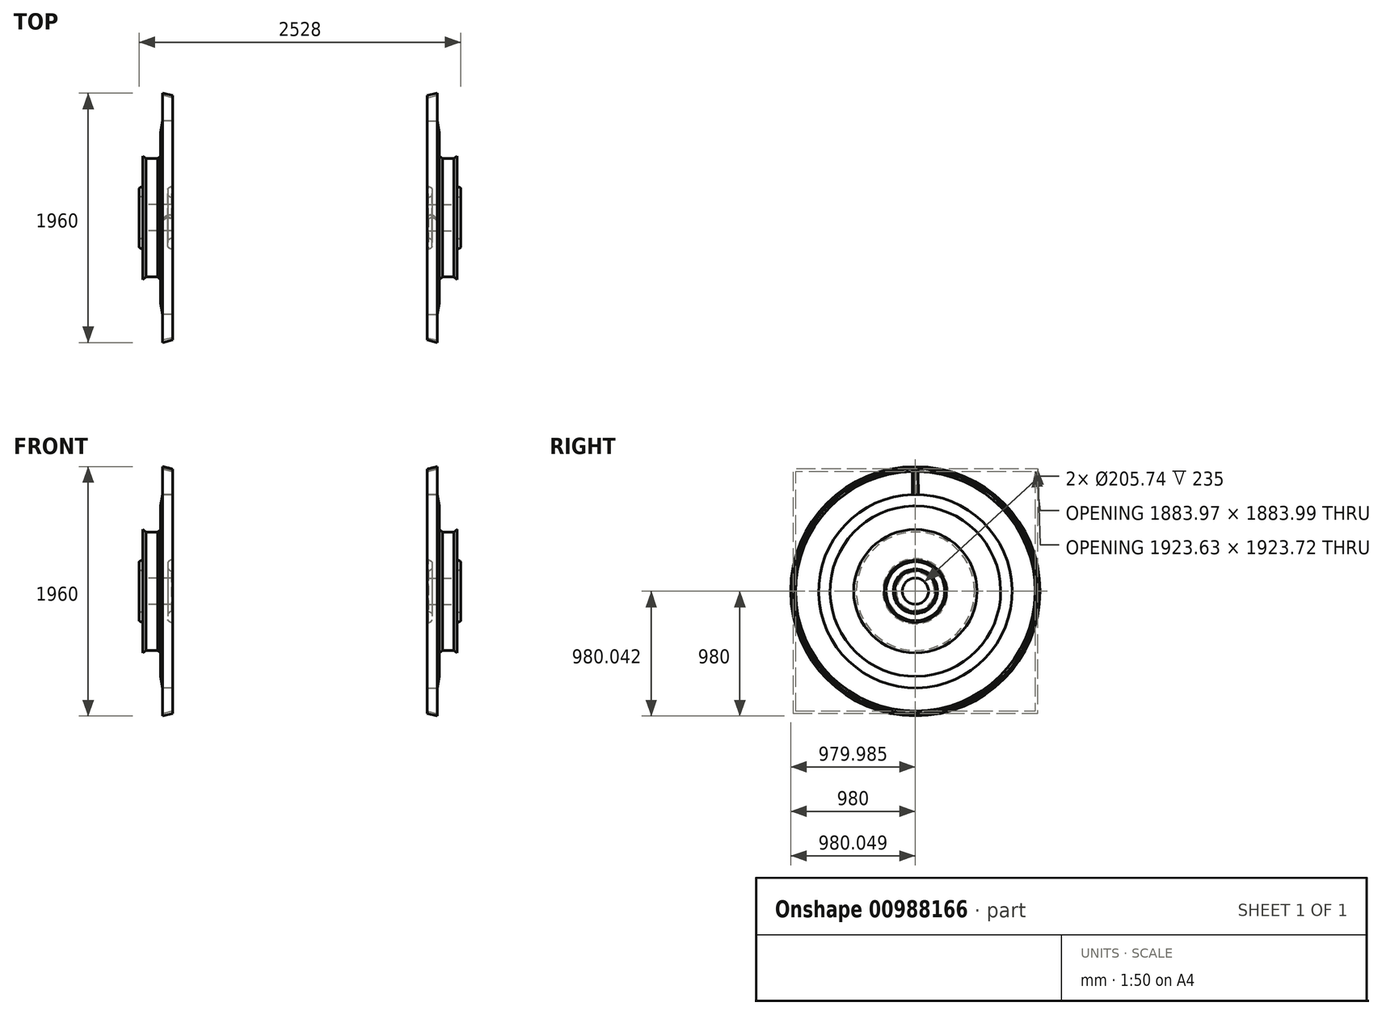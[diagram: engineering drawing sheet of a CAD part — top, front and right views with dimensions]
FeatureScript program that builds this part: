
annotation { "Feature Type Name" : "Feature", "Feature Type Description" : "" }
export const myFeature = defineFeature(function(context is Context, id is Id, definition is map)
    precondition{}
    {
        {
            var Q0;
            Q0=qCreatedBy(makeId("Top.planeOp"),FACE);
            var sketch = newSketch(context, id + "F0", { "sketchPlane" : qUnion([Q0])});
            skLineSegment(sketch, "E0", {"start": v(-458.73, 0) * mm, "end": v(0, 0) * mm, "construction": true});
            skLineSegment(sketch, "E1", {"start": v(0, 760) * mm, "end": v(-80, 760) * mm});
            skLineSegment(sketch, "E2", {"start": v(-120, 465) * mm, "end": v(-210, 465) * mm});
            skLineSegment(sketch, "E3", {"start": v(-210, 465) * mm, "end": v(-235, 485) * mm});
            skLineSegment(sketch, "E4", {"start": v(-235, 485) * mm, "end": v(-235, 243.87) * mm});
            skLineSegment(sketch, "E5", {"start": v(-235, 102.87) * mm, "end": v(0, 102.87) * mm});
            skLineSegment(sketch, "E6", {"start": v(0, 102.87) * mm, "end": v(0, 157.87) * mm});
            skLineSegment(sketch, "E7", {"start": v(-80, 980) * mm, "end": v(-80, 962) * mm});
            skLineSegment(sketch, "E8", {"start": v(-80, 962) * mm, "end": v(0, 942) * mm});
            skLineSegment(sketch, "E9", {"start": v(0, 942) * mm, "end": v(0, 960) * mm});
            skLineSegment(sketch, "E10", {"start": v(0, 960) * mm, "end": v(-80, 980) * mm});
            skLineSegment(sketch, "E11", {"start": v(-80, 760) * mm, "end": v(-80, 962) * mm, "construction": true});
            skLineSegment(sketch, "E12", {"start": v(-95, 485) * mm, "end": v(-95, 670) * mm});
            skLineSegment(sketch, "E13", {"start": v(-95, 670) * mm, "end": v(-80, 760) * mm});
            skLineSegment(sketch, "E14", {"start": v(-95, 485) * mm, "end": v(-120, 465) * mm});
            skLineSegment(sketch, "E15", {"start": v(-95, 485) * mm, "end": v(-235, 485) * mm, "construction": true});
            skArc(sketch, "E16", {"start": v(-235, 161.87) * mm, "mid": v(-250.7, 165) * mm, "end": v(-264, 173.89) * mm});
            skLineSegment(sketch, "E17", {"start": v(-264, 231.85) * mm, "end": v(-264, 173.89) * mm});
            skArc(sketch, "E18.trimOffspring", {"start": v(-264, 231.85) * mm, "mid": v(-250.7, 240.75) * mm, "end": v(-235, 243.87) * mm});
            skLineSegment(sketch, "E19.trimOffspring", {"start": v(-235, 161.87) * mm, "end": v(-235, 102.87) * mm});
            skArc(sketch, "E20", {"start": v(-235, 161.87) * mm, "mid": v(-276, 202.87) * mm, "end": v(-235, 243.87) * mm, "construction": true});
            skLineSegment(sketch, "E21", {"start": v(-235, 202.87) * mm, "end": v(0, 202.87) * mm, "construction": true});
            skArc(sketch, "E22", {"start": v(0, 157.87) * mm, "mid": v(-22.53, 163.91) * mm, "end": v(-39, 180.42) * mm});
            skLineSegment(sketch, "E23", {"start": v(-39, 225.32) * mm, "end": v(-39, 180.42) * mm});
            skArc(sketch, "E24.trimOffspring", {"start": v(-39, 225.32) * mm, "mid": v(-22.53, 241.83) * mm, "end": v(0, 247.87) * mm});
            skLineSegment(sketch, "E25.trimOffspring", {"start": v(0, 247.87) * mm, "end": v(0, 760) * mm});
            skArc(sketch, "E26", {"start": v(0, 157.87) * mm, "mid": v(-45, 202.87) * mm, "end": v(0, 247.87) * mm, "construction": true});
            skSolve(sketch);
        }
        {
            var Q0;
            Q0=makeQuery(id+"F0.imprint","IMPRINT",FACE,{"disambiguationData":[TD([[makeQuery(id+"F0.imprint","IMPRINT",EDGE,{"derivedFrom":sQuery(id+"F0.wireOp",EDGE,"E7")}),1.0]])]});
            var Q1;
            Q1=makeQuery(id+"F0.imprint","IMPRINT",FACE,{"disambiguationData":[TD([[makeQuery(id+"F0.imprint","IMPRINT",EDGE,{"derivedFrom":sQuery(id+"F0.wireOp",EDGE,"E1")}),1.0]])]});
            var Q2;
            Q2=sQuery(id+"F0.wireOp",EDGE,"E0");
            revolve(context, id + "F1", {"surfaceOperationType" : NewSurfaceOperationType.NEW, "entities" : qUnion([Q0, Q1]), "axis" : qUnion([Q2]), "revolveType" : RevolveType.FULL});
        }
        {
            var Q0;
            Q0=makeQuery(id+"F1.opRevolve","SWEPT_EDGE",EDGE,{"disambiguationData":[OSD([sQuery(id+"F0.wireOp",EDGE,"E24.trimOffspring"),sQuery(id+"F0.wireOp",EDGE,"E25.trimOffspring")])]});
            var Q1;
            Q1=makeQuery(id+"F1.opRevolve","SWEPT_EDGE",EDGE,{"disambiguationData":[OSD([sQuery(id+"F0.wireOp",EDGE,"E6"),sQuery(id+"F0.wireOp",EDGE,"E22")])]});
            chamfer(context, id + "F2", {"entities" : qUnion([Q0, Q1]), "width" : 9 * mm, "tangentPropagation" : true});
        }
        {
            var Q0;
            Q0=qCreatedBy(makeId("Right.planeOp"),FACE);
            var sketch = newSketch(context, id + "F3", { "sketchPlane" : qUnion([Q0])});
            skLineSegment(sketch, "E27", {"start": v(0, 0) * mm, "end": v(0, 760) * mm, "construction": true});
            skLineSegment(sketch, "E28", {"start": v(0, 0) * mm, "end": v(0, 960) * mm, "construction": true});
            skCircle(sketch, "E29.0", {"center": v(0, 0) * mm, "radius": 960 * mm, "construction": true});
            skCircle(sketch, "E30.0", {"center": v(0, 0) * mm, "radius": 760 * mm, "construction": true});
            skSolve(sketch);
        }
        {
            var Q0;
            Q0=qCreatedBy(makeId("Front.planeOp"),FACE);
            var sketch = newSketch(context, id + "F4", { "sketchPlane" : qUnion([Q0])});
            skLineSegment(sketch, "E31", {"start": v(-80, 980) * mm, "end": v(0, 960) * mm, "construction": true});
            skLineSegment(sketch, "E32", {"start": v(-40, 970) * mm, "end": v(-52.13, 921.5) * mm, "construction": true});
            skSolve(sketch);
        }
        {
            var Q0;
            Q0=sQuery(id+"F4.wireOp",VERTEX,"E32.start");
            var Q1;
            Q1=sQuery(id+"F4.wireOp",EDGE,"E32");
            cPlane(context, id + "F5", {"entities" : qUnion([Q0, Q1]), "cplaneType" : CPlaneType.LINE_POINT, "offset" : 25 * mm, "width" : 150 * mm, "height" : 150 * mm});
        }
        {
            var Q0;
            Q0=sQuery(id+"F3.wireOp",VERTEX,"E27.end");
            var Q1;
            Q1=sQuery(id+"F3.wireOp",EDGE,"E28");
            cPlane(context, id + "F6", {"entities" : qUnion([Q0, Q1]), "cplaneType" : CPlaneType.LINE_POINT, "offset" : 25 * mm, "width" : 150 * mm, "height" : 150 * mm});
        }
        {
            var Q0;
            Q0=qCreatedBy(id+"F6.planeOp",FACE);
            cPlane(context, id + "F7", {"entities" : qUnion([Q0]), "cplaneType" : CPlaneType.OFFSET, "offset" : 1 * mm, "oppositeDirection" : true, "width" : 150 * mm, "height" : 150 * mm});
        }
        {
            var Q0;
            Q0=qCreatedBy(id+"F5.planeOp",FACE);
            cPlane(context, id + "F8", {"entities" : qUnion([Q0]), "cplaneType" : CPlaneType.OFFSET, "offset" : 4 * mm, "width" : 150 * mm, "height" : 150 * mm});
        }
        {
            var Q0;
            Q0=qCreatedBy(id+"F7.planeOp",FACE);
            var sketch = newSketch(context, id + "F9", { "sketchPlane" : qUnion([Q0])});
            skLineSegment(sketch, "E33.0", {"start": v(-80, -760) * mm, "end": v(-80, 760) * mm, "construction": true});
            skLineSegment(sketch, "E34.0", {"start": v(0, 760) * mm, "end": v(0, -760) * mm, "construction": true});
            skLineSegment(sketch, "E35", {"start": v(0, 0) * mm, "end": v(0, 15) * mm});
            skLineSegment(sketch, "E36", {"start": v(-80, -11.9) * mm, "end": v(-80, -21.9) * mm});
            skFitSpline(sketch, "E37", {"points": [v(0, 15) * mm, v(-27.24, 23.1) * mm, v(-53.2, 15) * mm, v(-80, -11.9) * mm], "startDerivative": vector(-98.33, 77.82) * mm, "endDerivative": vector(-58.12, -78.29) * mm});
            skFitSpline(sketch, "E38", {"points": [v(0, 0) * mm, v(-12.16, -4.34) * mm, v(-33.61, 3.06) * mm, v(-80, -21.9) * mm], "startDerivative": vector(-36.35, -51.97) * mm, "endDerivative": vector(-93.61, -87.67) * mm});
            skSolve(sketch);
        }
        {
            var Q0;
            Q0=qCreatedBy(id+"F8.planeOp",FACE);
            var sketch = newSketch(context, id + "F10", { "sketchPlane" : qUnion([Q0])});
            skFitSpline(sketch, "E39", {"points": [v(-231.83, 3.95) * mm, v(-248.72, 5.12) * mm, v(-268.87, -2) * mm, v(-314.3, 23.8) * mm], "startDerivative": vector(-50.26, 54.8) * mm, "endDerivative": vector(-152.7, 116.62) * mm});
            skLineSegment(sketch, "E40", {"start": v(-314.3, -89.8) * mm, "end": v(-314.3, 89.8) * mm, "construction": true});
            skLineSegment(sketch, "E41", {"start": v(-231.83, 88.88) * mm, "end": v(-231.83, -88.88) * mm, "construction": true});
            skFitSpline(sketch, "E42", {"points": [v(-314.3, 13.8) * mm, v(-285.78, -12.5) * mm, v(-260.04, -21.06) * mm, v(-231.83, -11.05) * mm], "startDerivative": vector(54.34, -67.84) * mm, "endDerivative": vector(55.17, 74.14) * mm});
            skLineSegment(sketch, "E43", {"start": v(-231.83, -11.05) * mm, "end": v(-231.83, 3.95) * mm});
            skLineSegment(sketch, "E44", {"start": v(-314.3, 13.8) * mm, "end": v(-314.3, 23.8) * mm});
            skSolve(sketch);
        }
        {
            var Q2;
            Q2=qSketchRegion(id+"F9",true);
            var Q3;
            Q3=qSketchRegion(id+"F10",true);
            loft(context, id + "F11", {"operationType" : NewBodyOperationType.ADD, "sheetProfilesArray" : [{ "sheetProfileEntities" : qUnion([Q2]) }, { "sheetProfileEntities" : qUnion([Q3]) }]});
        }
        {
            var Q0;
            Q0=qCreatedBy(makeId("Right.planeOp"),FACE);
            cPlane(context, id + "F12", {"entities" : qUnion([Q0]), "cplaneType" : CPlaneType.OFFSET, "offset" : 1000 * mm, "width" : 150 * mm, "height" : 150 * mm});
        }
        {
            var Q0;
            Q0=makeQuery(id+"F1.opRevolve","SWEPT_BODY",BODY,{"disambiguationData":[OSD([sQuery(id+"F0.wireOp",EDGE,"E1"),sQuery(id+"F0.wireOp",EDGE,"E2"),sQuery(id+"F0.wireOp",EDGE,"E3"),sQuery(id+"F0.wireOp",EDGE,"E4"),sQuery(id+"F0.wireOp",EDGE,"E5"),sQuery(id+"F0.wireOp",EDGE,"E6"),sQuery(id+"F0.wireOp",EDGE,"E12"),sQuery(id+"F0.wireOp",EDGE,"E13"),sQuery(id+"F0.wireOp",EDGE,"E14"),sQuery(id+"F0.wireOp",EDGE,"E16"),sQuery(id+"F0.wireOp",EDGE,"E17"),sQuery(id+"F0.wireOp",EDGE,"E18.trimOffspring"),sQuery(id+"F0.wireOp",EDGE,"E19.trimOffspring"),sQuery(id+"F0.wireOp",EDGE,"E22"),sQuery(id+"F0.wireOp",EDGE,"E23"),sQuery(id+"F0.wireOp",EDGE,"E24.trimOffspring"),sQuery(id+"F0.wireOp",EDGE,"E25.trimOffspring")])]});
            var Q1;
            Q1=qCreatedBy(id+"F12.planeOp",FACE);
            mirror(context, id + "F13", {"entities" : qUnion([Q0]), "mirrorPlane" : qUnion([Q1])});
        }
    });
